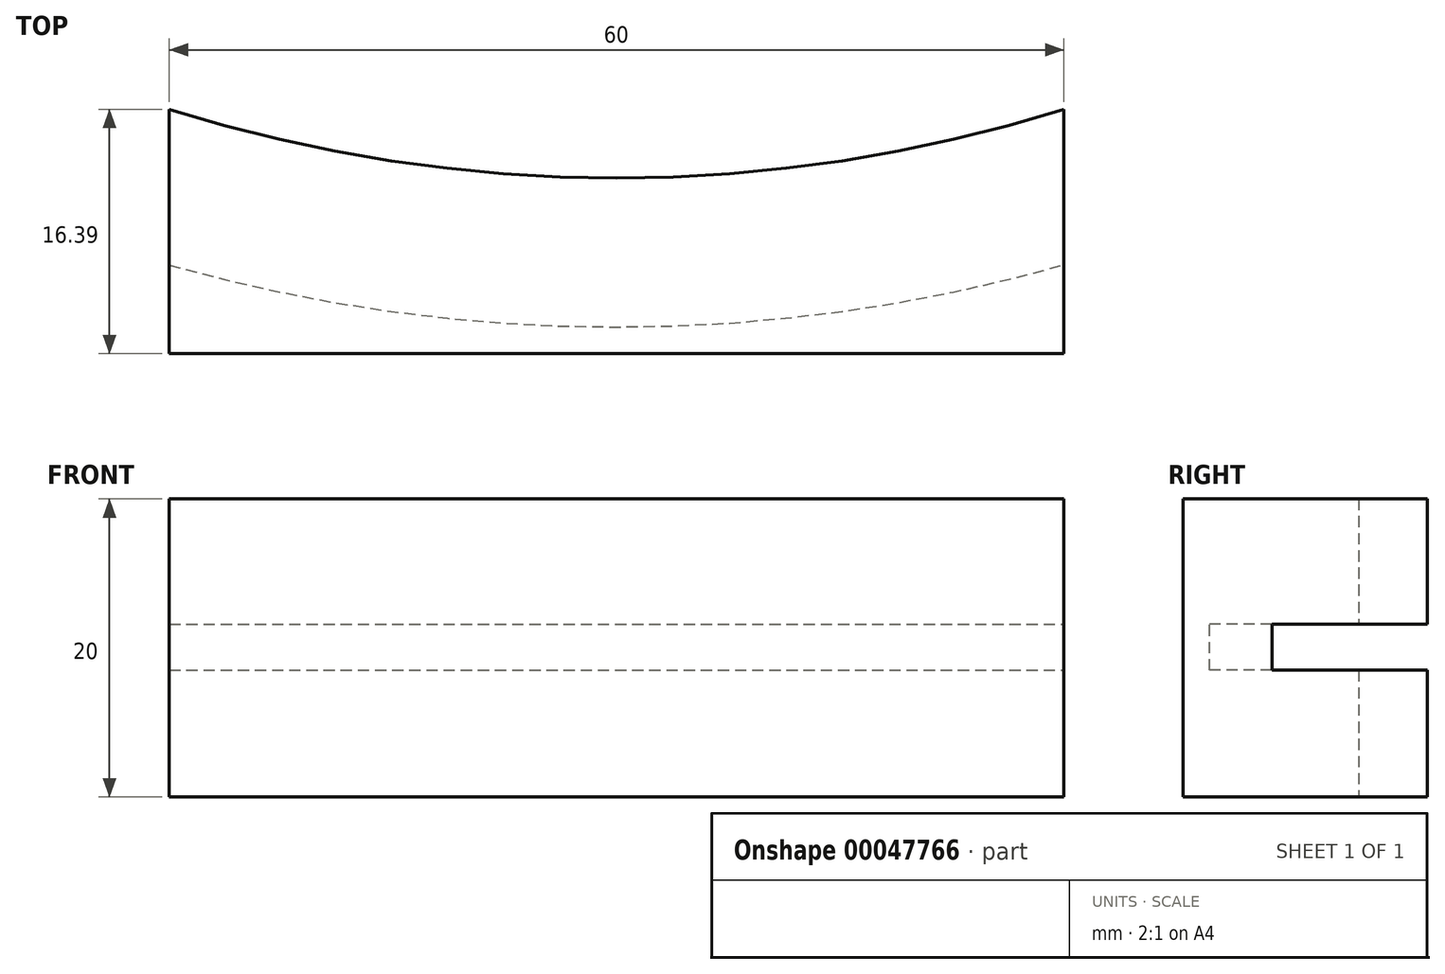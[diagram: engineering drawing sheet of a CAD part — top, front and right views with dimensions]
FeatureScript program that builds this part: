
annotation { "Feature Type Name" : "Feature", "Feature Type Description" : "" }
export const myFeature = defineFeature(function(context is Context, id is Id, definition is map)
    precondition{}
    {
        {
            var Q0;
            Q0=qCreatedBy(makeId("Top.planeOp"),FACE);
            var sketch = newSketch(context, id + "F0", { "sketchPlane" : qUnion([Q0])});
            skLineSegment(sketch, "E0.rect.bottom", {"start": v(30, 10) * mm, "end": v(-30, 10) * mm});
            skLineSegment(sketch, "E0.rect.top", {"start": v(30, -10) * mm, "end": v(-30, -10) * mm});
            skLineSegment(sketch, "E0.rect.left", {"start": v(30, 10) * mm, "end": v(30, -10) * mm});
            skLineSegment(sketch, "E0.rect.right", {"start": v(-30, 10) * mm, "end": v(-30, -10) * mm});
            skPoint(sketch, "E0.rect.middle", {"position": v(0, 0) * mm});
            skCircle(sketch, "E1", {"center": v(0, 102.56) * mm, "radius": 100 * mm});
            skSolve(sketch);
        }
        {
            var Q0;
            {var subQ0=sQuery(id+"F0.wireOp",EDGE,"E0.rect.top");Q0=makeQuery(id+"F0.imprint","IMPRINT",FACE,{"disambiguationData":[TD([[makeQuery(id+"F0.imprint","IMPRINT",EDGE,{"derivedFrom":subQ0}),-1.0]])]});}
            extrude(context, id + "F1", {"entities" : qUnion([Q0]), "depth" : 20 * mm});
        }
        {
            var Q0;
            Q0=qCreatedBy(makeId("Top.planeOp"),FACE);
            cPlane(context, id + "F2", {"entities" : qUnion([Q0]), "cplaneType" : CPlaneType.OFFSET, "offset" : 10 * mm, "width" : 150 * mm, "height" : 150 * mm});
        }
        {
            var Q0;
            Q0=qCreatedBy(id+"F2.planeOp",FACE);
            var sketch = newSketch(context, id + "F5", { "sketchPlane" : qUnion([Q0])});
            skCircle(sketch, "E2", {"center": v(0, 102.56) * mm, "radius": 110 * mm});
            skSolve(sketch);
        }
        {
            var Q0;
            Q0=qCreatedBy(makeId("Right.planeOp"),FACE);
            var sketch = newSketch(context, id + "F6", { "sketchPlane" : qUnion([Q0])});
            skLineSegment(sketch, "E3.bottom", {"start": v(4.56, 11.6) * mm, "end": v(-7.44, 11.6) * mm});
            skLineSegment(sketch, "E3.top", {"start": v(4.56, 8.5) * mm, "end": v(-7.44, 8.5) * mm});
            skLineSegment(sketch, "E3.left", {"start": v(4.56, 11.6) * mm, "end": v(4.56, 8.5) * mm});
            skLineSegment(sketch, "E3.right", {"start": v(-7.44, 11.6) * mm, "end": v(-7.44, 8.5) * mm});
            skSolve(sketch);
        }
        {
            var Q0;
            Q0=makeQuery(id+"F6.imprint","IMPRINT",FACE,{"disambiguationData":[TD([[makeQuery(id+"F6.imprint","IMPRINT",EDGE,{"derivedFrom":sQuery(id+"F6.wireOp",EDGE,"E3.bottom")}),1.0]])]});
            var Q1;
            Q1 = qBodyType(qCreatedBy(id + "F5" ,EDGE), BodyType.WIRE);
            revolve(context, id + "F7", {"operationType" : NewBodyOperationType.REMOVE, "entities" : qUnion([Q0]), "axis" : qUnion([Q1]), "revolveType" : RevolveType.FULL, "oppositeDirection" : true});
        }
        {
            var Q0;
            Q0=makeQuery(id+"F1.opExtrude","CAP_FACE",FACE,{"disambiguationData":[OSD([sQuery(id+"F0.wireOp",EDGE,"E0.rect.top"),sQuery(id+"F0.wireOp",EDGE,"E0.rect.left"),sQuery(id+"F0.wireOp",EDGE,"E0.rect.right"),sQuery(id+"F0.wireOp",EDGE,"E1")])],"isStart":false});
            var sketch = newSketch(context, id + "F3", { "sketchPlane" : qUnion([Q0])});
            skLineSegment(sketch, "E4.bottom", {"start": v(-30, -10) * mm, "end": v(30, -10) * mm});
            skLineSegment(sketch, "E4.top", {"start": v(-30, -9.23) * mm, "end": v(30, -9.23) * mm});
            skLineSegment(sketch, "E4.left", {"start": v(-30, -10) * mm, "end": v(-30, -9.23) * mm});
            skLineSegment(sketch, "E4.right", {"start": v(30, -10) * mm, "end": v(30, -9.23) * mm});
            skSolve(sketch);
        }
        {
            var Q0;
            Q0 = qSketchRegion(id + "F3", true);
            extrude(context, id + "F4", {"entities" : qUnion([Q0]), "operationType" : NewBodyOperationType.REMOVE, "oppositeDirection" : true, "depth" : 25 * mm});
        }
    });
